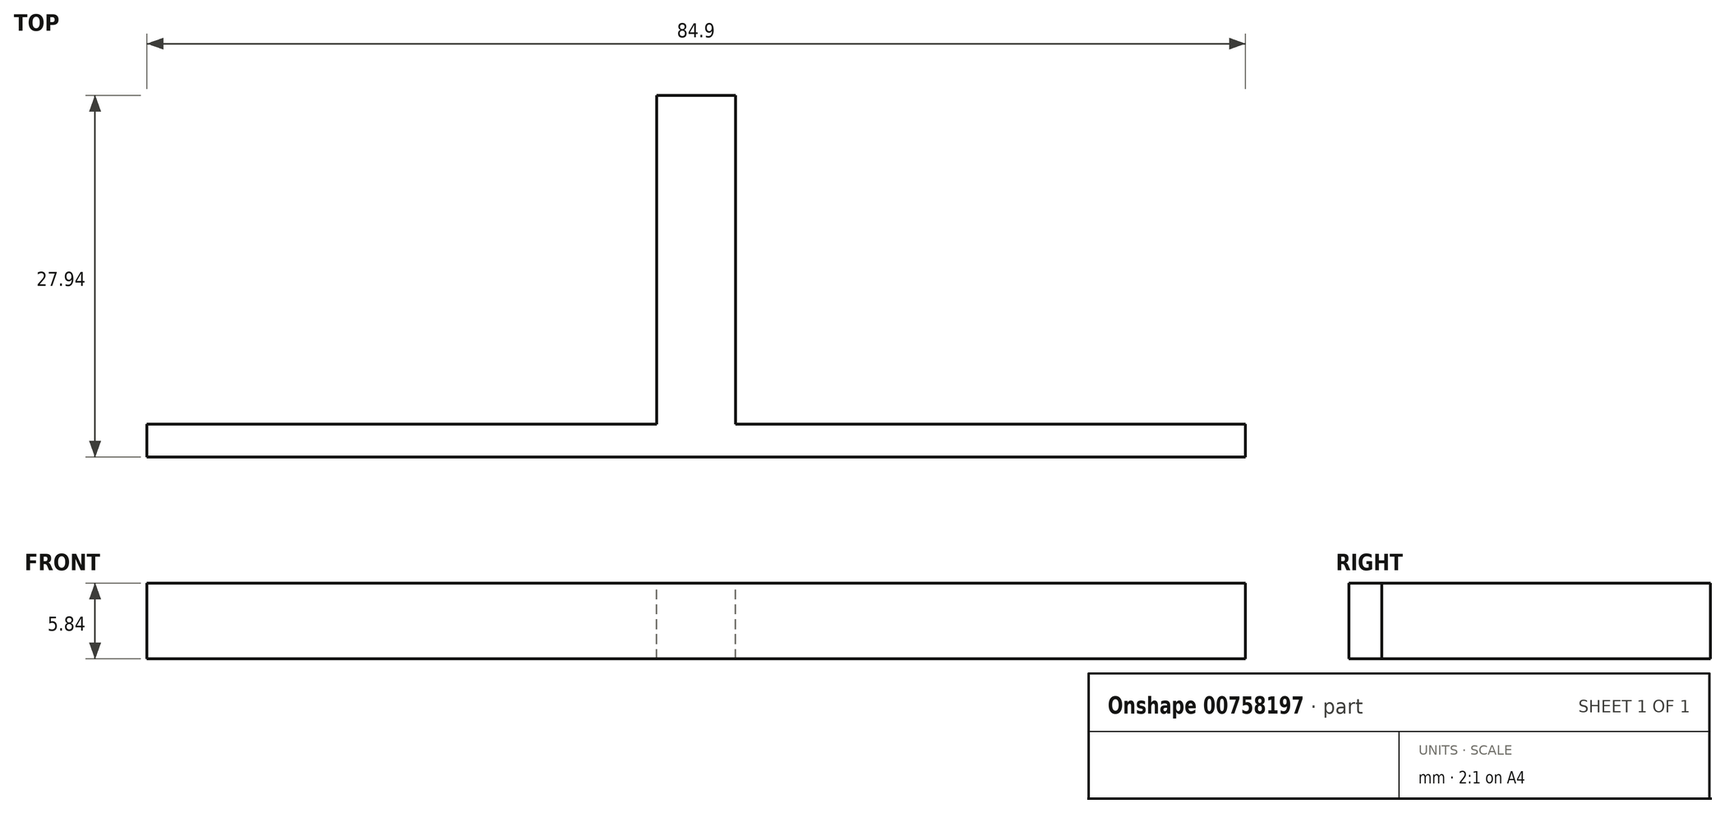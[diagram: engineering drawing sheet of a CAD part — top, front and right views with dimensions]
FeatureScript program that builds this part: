
annotation { "Feature Type Name" : "Feature", "Feature Type Description" : "" }
export const myFeature = defineFeature(function(context is Context, id is Id, definition is map)
    precondition{}
    {
        {
            var Q0;
            Q0=qCreatedBy(makeId("Front.planeOp"),FACE);
            var sketch = newSketch(context, id + "F0", { "sketchPlane" : qUnion([Q0])});
            skLineSegment(sketch, "E0.bottom", {"start": v(3.04, -2.92) * mm, "end": v(-3.04, -2.92) * mm});
            skLineSegment(sketch, "E0.top", {"start": v(3.04, 2.92) * mm, "end": v(-3.04, 2.92) * mm});
            skLineSegment(sketch, "E0.left", {"start": v(3.04, -2.92) * mm, "end": v(3.04, 2.92) * mm});
            skLineSegment(sketch, "E0.right", {"start": v(-3.04, -2.92) * mm, "end": v(-3.04, 2.92) * mm});
            skPoint(sketch, "E0.middle", {"position": v(0, 0) * mm});
            skSolve(sketch);
        }
        {
            var Q0;
            Q0=makeQuery(id+"F0.imprint","IMPRINT",FACE,{"disambiguationData":[TD([[makeQuery(id+"F0.imprint","IMPRINT",EDGE,{"derivedFrom":sQuery(id+"F0.wireOp",EDGE,"E0.bottom")}),-1.0]])]});
            extrude(context, id + "F1", {"entities" : qUnion([Q0]), "depth" : 25.4 * mm, "offsetDistance" : 25.4 * mm});
        }
        {
            var Q0;
            Q0=makeQuery(id+"F1.opExtrude","CAP_FACE",FACE,{"disambiguationData":[OSD([sQuery(id+"F0.wireOp",EDGE,"E0.bottom"),sQuery(id+"F0.wireOp",EDGE,"E0.top"),sQuery(id+"F0.wireOp",EDGE,"E0.left"),sQuery(id+"F0.wireOp",EDGE,"E0.right")])],"isStart":false});
            var sketch = newSketch(context, id + "F2", { "sketchPlane" : qUnion([Q0])});
            skLineSegment(sketch, "E1.bottom", {"start": v(42.45, -2.92) * mm, "end": v(-42.45, -2.92) * mm});
            skLineSegment(sketch, "E1.top", {"start": v(42.45, 2.92) * mm, "end": v(-42.45, 2.92) * mm});
            skLineSegment(sketch, "E1.left", {"start": v(42.45, -2.92) * mm, "end": v(42.45, 2.92) * mm});
            skLineSegment(sketch, "E1.right", {"start": v(-42.45, -2.92) * mm, "end": v(-42.45, 2.92) * mm});
            skPoint(sketch, "E1.middle", {"position": v(0, 0) * mm});
            skSolve(sketch);
        }
        {
            var Q0;
            {var subQ1=makeQuery(id+"F1.opExtrude","CAP_EDGE",EDGE,{"disambiguationData":[OSD([sQuery(id+"F0.wireOp",EDGE,"E0.left")])],"isStart":false});Q0=makeQuery(id+"F2.imprint","IMPRINT",FACE,{"disambiguationData":[TD([[makeQuery(id+"F2.imprint","IMPRINT",EDGE,{"derivedFrom":subQ1}),1.0]])]});}
            var Q1;
            {var subQ2=sQuery(id+"F2.wireOp",EDGE,"E1.left");Q1=makeQuery(id+"F2.imprint","IMPRINT",FACE,{"disambiguationData":[TD([[makeQuery(id+"F2.imprint","IMPRINT",EDGE,{"derivedFrom":subQ2}),1.0]])]});}
            var Q2;
            {var subQ2=sQuery(id+"F2.wireOp",EDGE,"E1.right");Q2=makeQuery(id+"F2.imprint","IMPRINT",FACE,{"disambiguationData":[TD([[makeQuery(id+"F2.imprint","IMPRINT",EDGE,{"derivedFrom":subQ2}),-1.0]])]});}
            extrude(context, id + "F3", {"entities" : qUnion([Q0, Q1, Q2]), "operationType" : NewBodyOperationType.ADD, "depth" : 2.54 * mm, "offsetDistance" : 25.4 * mm});
        }
    });
